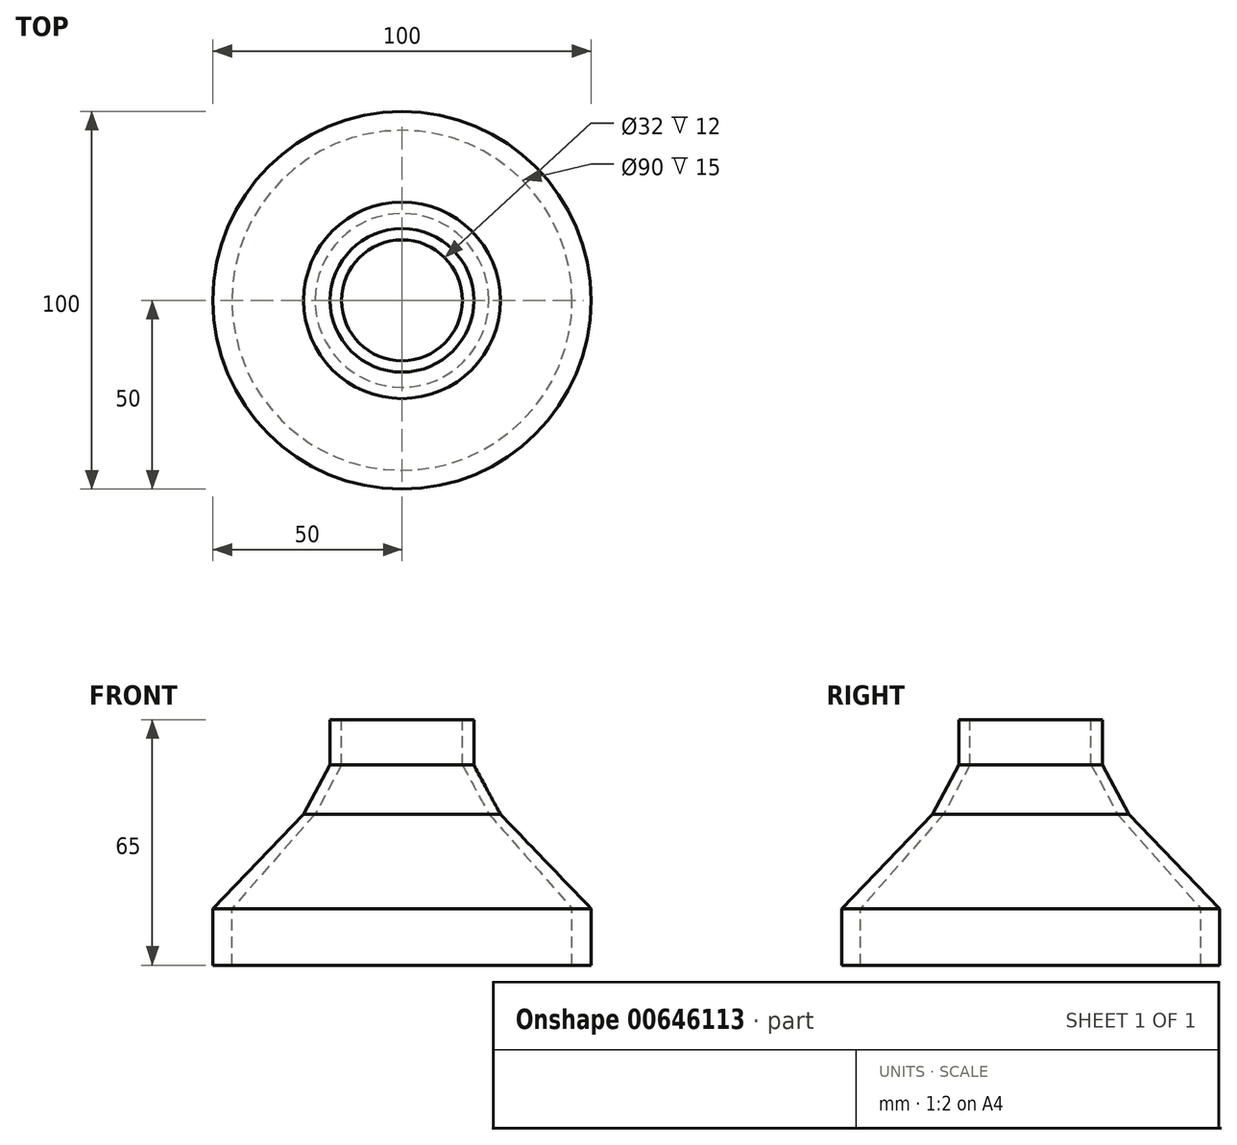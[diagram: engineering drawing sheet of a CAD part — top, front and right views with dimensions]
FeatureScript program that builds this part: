
annotation { "Feature Type Name" : "Feature", "Feature Type Description" : "" }
export const myFeature = defineFeature(function(context is Context, id is Id, definition is map)
    precondition{}
    {
        {
            var Q0;
            Q0=qCreatedBy(makeId("Front.planeOp"),FACE);
            var sketch = newSketch(context, id + "F0", { "sketchPlane" : qUnion([Q0])});
            skLineSegment(sketch, "E0", {"start": v(-19, 50) * mm, "end": v(-19, 38) * mm});
            skLineSegment(sketch, "E1", {"start": v(-19, 38) * mm, "end": v(-26, 25) * mm});
            skLineSegment(sketch, "E2", {"start": v(-26, 25) * mm, "end": v(-50, 0) * mm});
            skLineSegment(sketch, "E3.left", {"start": v(-50, 0) * mm, "end": v(-50, 0) * mm});
            skLineSegment(sketch, "E4", {"start": v(-23, 25) * mm, "end": v(-16, 38) * mm});
            skLineSegment(sketch, "E5", {"start": v(-16, 38) * mm, "end": v(-16, 50) * mm});
            skLineSegment(sketch, "E6", {"start": v(-16, 50) * mm, "end": v(-19, 50) * mm});
            skLineSegment(sketch, "E7", {"start": v(0, 69.2) * mm, "end": v(0, -18.8) * mm, "construction": true});
            skLineSegment(sketch, "E8", {"start": v(-23, 25) * mm, "end": v(-45, 0) * mm});
            skLineSegment(sketch, "E9", {"start": v(-50, 0) * mm, "end": v(-50, -15) * mm});
            skLineSegment(sketch, "E10", {"start": v(-50, -15) * mm, "end": v(-45, -15) * mm});
            skLineSegment(sketch, "E11", {"start": v(-45, -15) * mm, "end": v(-45, 0) * mm});
            skSolve(sketch);
        }
        {
            var Q0;
            Q0=makeQuery(id+"F0.imprint","IMPRINT",FACE,{"disambiguationData":[TD([[makeQuery(id+"F0.imprint","IMPRINT",EDGE,{"derivedFrom":sQuery(id+"F0.wireOp",EDGE,"E0")}),1.0]])]});
            var Q1;
            Q1=sQuery(id+"F0.wireOp",EDGE,"E7");
            revolve(context, id + "F1", {"entities" : qUnion([Q0]), "axis" : qUnion([Q1]), "revolveType" : RevolveType.FULL});
        }
    });
